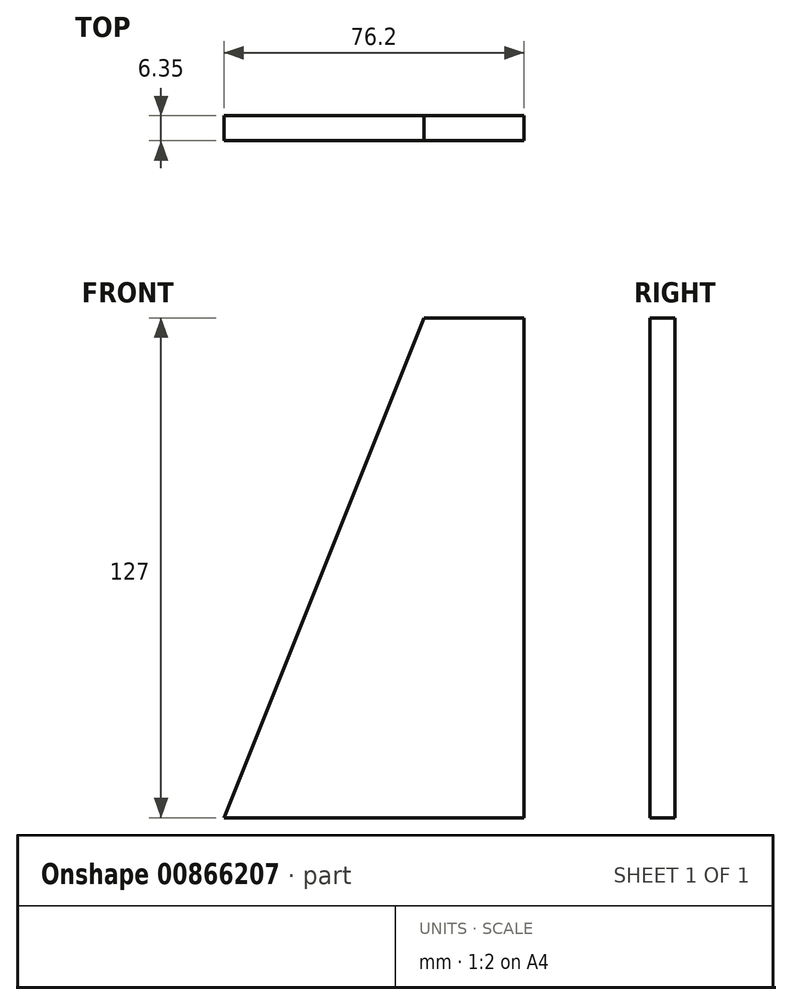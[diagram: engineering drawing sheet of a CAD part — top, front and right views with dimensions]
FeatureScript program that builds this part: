
annotation { "Feature Type Name" : "Feature", "Feature Type Description" : "" }
export const myFeature = defineFeature(function(context is Context, id is Id, definition is map)
    precondition{}
    {
        {
            var Q0;
            Q0=qCreatedBy(makeId("Front.planeOp"),FACE);
            var sketch = newSketch(context, id + "F0", { "sketchPlane" : qUnion([Q0])});
            skLineSegment(sketch, "E0", {"start": v(0, 0) * mm, "end": v(-76.2, 0) * mm});
            skLineSegment(sketch, "E1", {"start": v(0, 0) * mm, "end": v(0, 127) * mm});
            skLineSegment(sketch, "E2", {"start": v(0, 127) * mm, "end": v(-25.4, 127) * mm});
            skLineSegment(sketch, "E3", {"start": v(-25.4, 127) * mm, "end": v(-76.2, 0) * mm});
            skSolve(sketch);
        }
        {
            var Q0;
            Q0=makeQuery(id+"F0.imprint","IMPRINT",FACE,{"disambiguationData":[TD([[makeQuery(id+"F0.imprint","IMPRINT",EDGE,{"derivedFrom":sQuery(id+"F0.wireOp",EDGE,"E0")}),-1.0]])]});
            extrude(context, id + "F1", {"entities" : qUnion([Q0]), "depth" : 6.35 * mm, "offsetDistance" : 25.4 * mm});
        }
    });
